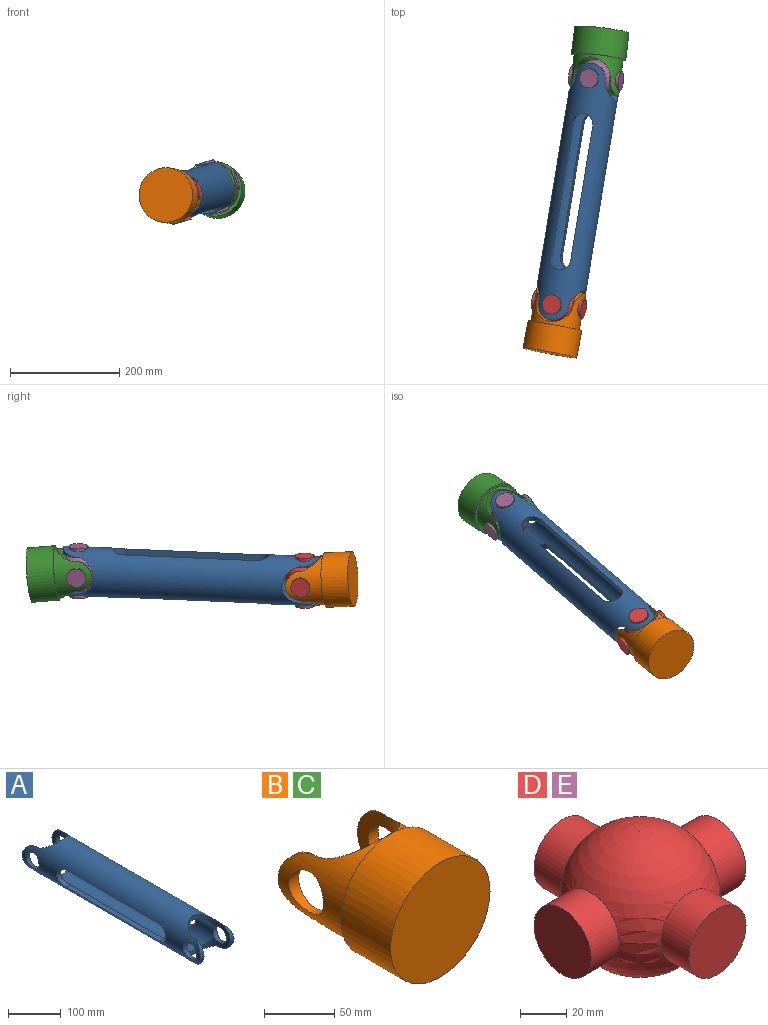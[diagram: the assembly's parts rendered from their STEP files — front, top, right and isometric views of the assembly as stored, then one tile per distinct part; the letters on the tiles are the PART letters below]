
ASSEMBLY  parts=5 mates=3
PART A: 26 faces, bbox 90x476.6x90 mm
  f0: cylinder r=45mm len=476.57mm, axis (0,1,0), area 88359.1mm2, adj f2,f3,f6,f7,f8,f9,f10,f11
  f1: cylinder r=35mm len=395.25mm, axis (0,1,0), area 57669.8mm2, adj f2,f3,f6,f7,f8,f9,f10,f11
  f2: cylinder r=35mm len=70mm, axis (0,0,1), area 1388.1mm2, adj f0,f1,f20,f21,f22,f23
  f3: cylinder r=35mm len=70mm, axis (0,0,1), area 1388.1mm2, adj f0,f1,f20,f21,f22,f23
  f4: plane 56.57x28.28mm, normal (-1,0,0), area 775.6mm2, adj f14,f15,f17,f19
  f5: plane 56.57x28.28mm, normal (1,0,0), area 775.6mm2, adj f14,f15,f16,f18
  f6: plane 250x11.59mm, normal (0,0,1), area 2897.1mm2, adj f0,f1,f7,f9
  f7: cylinder r=20mm len=40mm, axis (-1,0,0), area 675.4mm2, adj f0,f1,f6,f8
  f8: plane 250x11.59mm, normal (0,0,-1), area 2897.1mm2, adj f0,f1,f7,f9
  f9: cylinder r=20mm len=40mm, axis (-1,0,0), area 675.4mm2, adj f0,f1,f6,f8
  f10: cylinder r=20mm len=40mm, axis (-1,0,0), area 675.4mm2, adj f0,f1,f11,f13
  f11: plane 250x11.59mm, normal (0,0,-1), area 2897.1mm2, adj f0,f1,f10,f12
  f12: cylinder r=20mm len=40mm, axis (-1,0,0), area 675.4mm2, adj f0,f1,f11,f13
  f13: plane 250x11.59mm, normal (0,0,1), area 2897.1mm2, adj f0,f1,f10,f12
  f14: cylinder r=35mm len=70mm, axis (0,0,1), area 1388.1mm2, adj f0,f1,f4,f5,f16,f17
  f15: cylinder r=35mm len=70mm, axis (0,0,1), area 1388.1mm2, adj f0,f1,f4,f5,f16,f17
  f16: cylinder r=17.5mm len=35mm, axis (1,0,0), area 951.1mm2, adj f0,f1,f5,f14,f15
  f17: cylinder r=17.5mm len=35mm, axis (1,0,0), area 951.9mm2, adj f0,f1,f4,f14,f15
  f18: cylinder r=28.28mm len=56.57mm, axis (1,0,0), area 458.2mm2, adj f0,f5
  f19: cylinder r=28.28mm len=56.57mm, axis (1,0,0), area 458.1mm2, adj f0,f4
  f20: plane 56.57x28.28mm, normal (-1,0,0), area 775.6mm2, adj f2,f3,f23,f25
  f21: plane 56.57x28.28mm, normal (1,0,0), area 775.6mm2, adj f2,f3,f22,f24
  f22: cylinder r=17.5mm len=35mm, axis (1,0,0), area 951.9mm2, adj f0,f1,f2,f3,f21
  f23: cylinder r=17.5mm len=35mm, axis (1,0,0), area 951.1mm2, adj f0,f1,f2,f3,f20
  f24: cylinder r=28.28mm len=56.57mm, axis (1,0,0), area 458.1mm2, adj f0,f21
  f25: cylinder r=28.28mm len=56.57mm, axis (1,0,0), area 458.2mm2, adj f0,f20
PART B: 11 faces, bbox 100x118.3x100 mm
  f0: cylinder r=45mm len=90mm, axis (0,-1,0), area 7768.4mm2, adj f4,f6,f7,f8,f9,f10
  f1: plane 56.57x28.28mm, normal (-1,0,0), area 775.6mm2, adj f6,f9,f10
  f2: plane 56.57x28.28mm, normal (1,0,0), area 775.6mm2, adj f6,f7,f8
  f3: cylinder r=50mm len=100mm, axis (0,-1,0), area 15708mm2, adj f4,f5
  f4: plane 100x100mm, normal (0,1,0), area 1492.3mm2, adj f0,f3
  f5: plane 100x100mm, normal (0,-1,0), area 7854mm2, adj f3
  f6: cylinder r=35mm len=90mm, axis (0,0,1), area 7167.4mm2, adj f0,f1,f2,f8,f10
  f7: cylinder r=28.28mm len=56.57mm, axis (1,0,0), area 458.2mm2, adj f0,f2
  f8: cylinder r=17.5mm len=35mm, axis (1,0,0), area 1033.1mm2, adj f0,f2,f6
  f9: cylinder r=28.28mm len=56.57mm, axis (1,0,0), area 458.1mm2, adj f0,f1
  f10: cylinder r=17.5mm len=35mm, axis (1,0,0), area 1033.8mm2, adj f0,f1,f6
PART C: same geometry as B
PART D: 9 faces, bbox 95x95x70 mm
  f0: sphere r=35mm, area 11269mm2, adj f1,f4,f6,f7
  f1: cylinder r=17.5mm len=35mm, axis (0,1,0), area 1890mm2, adj f0,f2
  f2: plane 35x35mm, normal (0,1,0), area 962.1mm2, adj f1
  f3: plane 35x35mm, normal (0,-1,0), area 962.1mm2, adj f4
  f4: cylinder r=17.5mm len=35mm, axis (0,1,0), area 1890mm2, adj f0,f3
  f5: plane 35x35mm, normal (1,0,0), area 962.1mm2, adj f6
  f6: cylinder r=17.5mm len=35mm, axis (-1,0,0), area 1890mm2, adj f0,f5
  f7: cylinder r=17.5mm len=35mm, axis (-1,0,0), area 1890mm2, adj f0,f8
  f8: plane 35x35mm, normal (-1,0,0), area 962.1mm2, adj f7
PART E: same geometry as D
PLACE A rot(axis=(0.11,0.99,-0.09),74.5deg) t=(-94.99,476.18,77.48)mm
PLACE B rot(axis=(0.09,1,-0.03),164.4deg) t=(-185.92,-65.76,61.37)mm
PLACE C rot(axis=(-0.14,0.05,0.99),173.8deg) t=(-90.7,525.79,68.45)mm
PLACE D rot(axis=(-0.5,-0.56,-0.66),134.5deg) t=(-169.38,22.65,58.07)mm
PLACE E rot(axis=(-0.49,-0.59,-0.64),132.4deg) t=(-101.45,436.74,75.79)mm
MATE revolute E.f6 <-> A.f16  axis (-0.28,0,0.96) through (-111.13,436.89,109.43)mm
MATE fastened D.f6 <-> A.f22  axis (-0.28,0,0.96) through (-179.05,22.8,91.7)mm
MATE revolute D.f1 <-> B.f7  axis (0.95,-0.17,0.27) through (-136.22,16.8,67.63)mm
